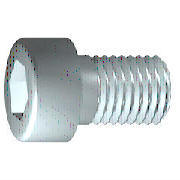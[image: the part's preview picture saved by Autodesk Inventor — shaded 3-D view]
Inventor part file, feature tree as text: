
AUTODESK INVENTOR PART (.ipt)
format: ipt  version: 2023.3 (Build 273359000, 359)  size: 194,048 bytes
history: native  units: mm (DEFAULTED — no unit token found)
features: sketch x2, other x1, extrude x1, plane x1, fillet x1
ambient origin geometry x7: Origin, YZ Plane, XY Plane, X Axis, Y Axis, Z Axis, Center Point
bodies: Solid1 (feature_tree)
feature tree (6):
  other  "Körper"
  extrude  "Loch"  Depth=3.0mm
  plane  "Work Plane1"
  fillet  "Fillet2"  Radius=3.0mm
  sketch  "Skizze1"  dims[d1=4.75mm d2=0.306825mm d3=3.0mm]
  sketch  "Skizze2"  dims[d4=1.3mm d5=60.0deg d6=3.0mm d7=3.0mm d8=2.886751mm d9=5.5mm d10=90.0deg d11=10.0mm d12=0.0mm d13=4.75mm d14=0.0mm d15=0.306725mm d16=0.306725mm d17=0.3mm d19=0.0mm d26=6.0mm d27=45.0deg d28=0.0mm d29=0.0mm d30=0.1mm]
